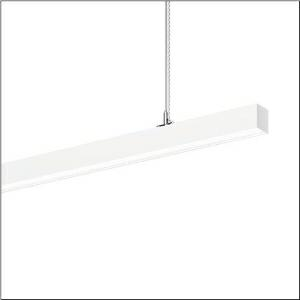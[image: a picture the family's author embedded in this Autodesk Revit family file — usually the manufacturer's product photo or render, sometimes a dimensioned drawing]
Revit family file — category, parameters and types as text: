
# Revit family: silica_r__21_51mx33dc4dwb_294c
name_source: partatom
category: Lighting Fixtures
units: mm (PartAtom-declared; Revit-internal decimal feet)

## family parameters
Cut with Voids When Loaded = No
Host = Face
Light Source = No
Part Type = Normal
Room Calculation Point = No
Round Connector Dimension = Use Diameter
Shared = No

## types (1)
- --- (1 x LED, 14790 lm, 93.9 W, 4000K)
    Apparent Load = 94 VA
    CIE Flux Codes = 78 96 99 55 100
    Color Rendering = 80
    Color Temperature = 4000K
    Default Elevation = 1800 mm
    Description = Silica® 21, office luminaire, primary optical cover: prismatic diffuser, of PMMA, CAT 2 (L<= 3000cd/m²), light emission: direct/indirect distribution, primary light characteristic: symmetric, installation type: suspended mounting, LED, rated luminous flux: 14.790lm, luminous efficacy: 158lm/W, light colour: 840, colour temperature: 4000K, control gear: DALI 2, with terminal, 3+2-pole, max. 2.5mm², mains connection: 220..240V, AC, 50/60Hz, rated input power: 93.9W, luminaire housing, of aluminium, traffic white (RAL 9016), length: 3.004mm, width: 53mm, height: 53mm, protection rating (complete): IP20, insulation class (complete): insulation class I (protective earthing), certification: CE, permissible operating ambient temperature: 0..+35°C, standard: EN 50419, packaging unit: 1 piece
    Height = 53 mm
    Lamp = 1 x LED
    Lamp Light Flux = 14790 lm
    Lamp Power = 93.9 W
    Lamp count = 1
    Length = 3004 mm
    Luminous efficacy = 158 lm/W
    Manufacturer = Siteco
    ModVariant = No
    Model = 51MX33DC4DWB
    Mounting Place = Ceiling
    Mounting Type = Pendant
    Number of Poles = 1
    OnlyDefault = Yes
    Power Factor = 1
    Product Name = Silica® 21
    Product group = office luminaire | ceiling pendant
    ProductGroupID = 904
    Protection Class = Protection class I
    Protection Degree = IP 20
    RLX_Detail_Level = 1
    RLX_Emergency_Light_Flux = 0 lm
    RLX_Emergency_Type = 0
    RLX_Emergency_Type_DB = No
    RlxData = <blob elided: 21417 chars, md5=d9eb8264>
    Socket = socket
    Standby Power = 0 W
    System Light Flux = 14790 lm
    System Power = 94 W
    Type Comments = factory setting: luminous flux: 100 % | dim-lin: 254 | 323 mA
    Type Image = l_1349007.jpg
    URL = http://relux.com
    VarID = @adj_118836
    Voltage = 0 V
    Weight = 0.00 kg
    Width = 53 mm

## geometry (parser evidence)
native form markers: Blend x4, Sweep x12
no freeform markers — native parametric forms only
